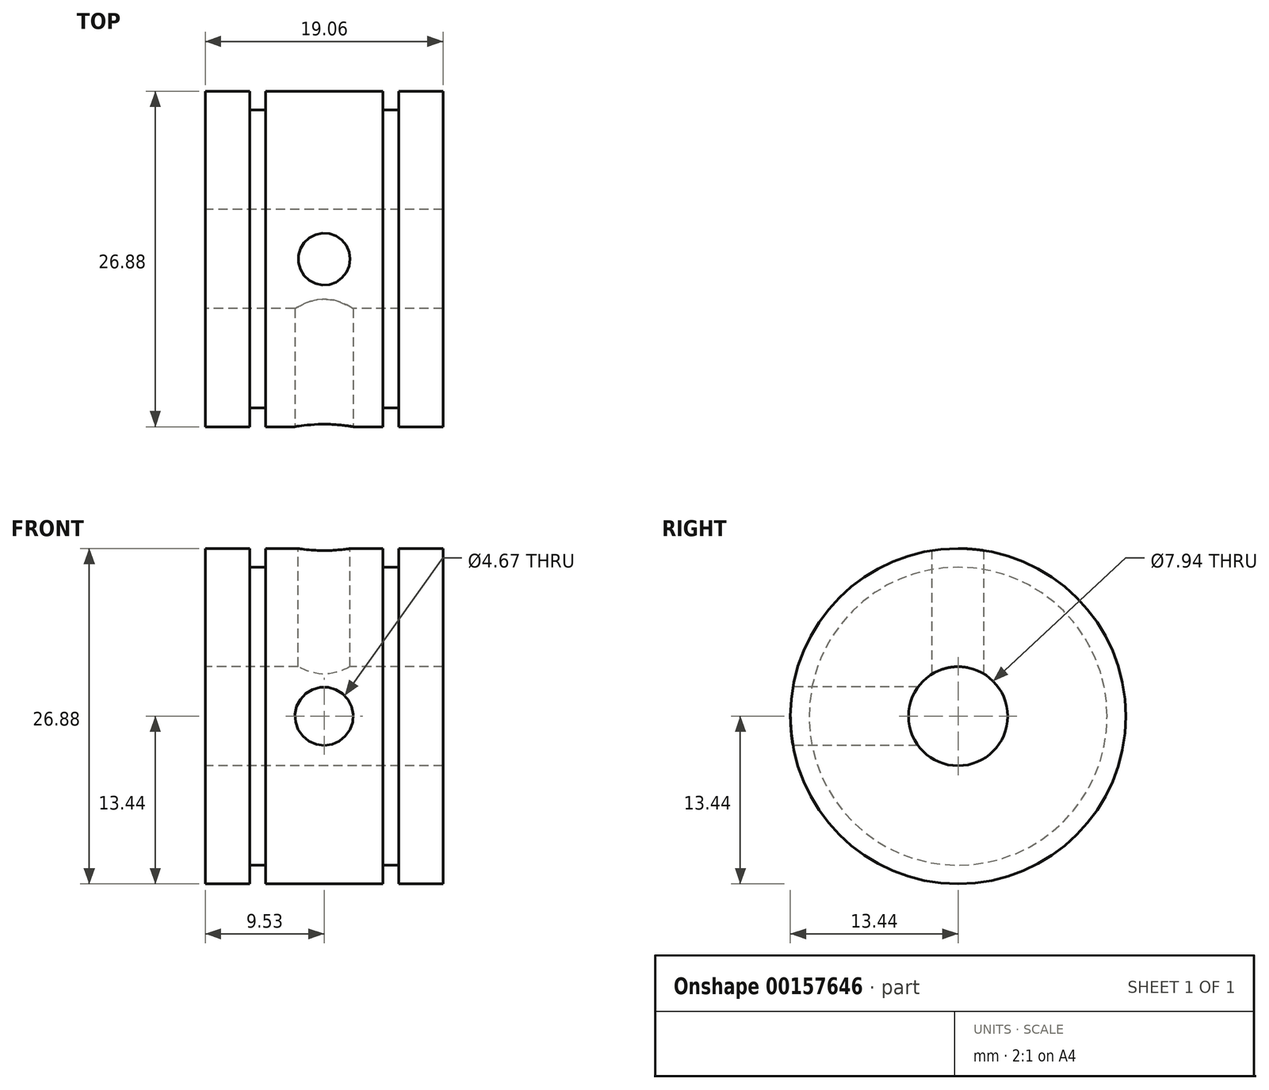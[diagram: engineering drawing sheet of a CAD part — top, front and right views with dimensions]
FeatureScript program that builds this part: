
annotation { "Feature Type Name" : "Feature", "Feature Type Description" : "" }
export const myFeature = defineFeature(function(context is Context, id is Id, definition is map)
    precondition{}
    {
        {
            var Q0;
            Q0=qCreatedBy(makeId("Right.planeOp"),FACE);
            var sketch = newSketch(context, id + "F0", { "sketchPlane" : qUnion([Q0])});
            skCircle(sketch, "E0", {"center": v(0, 0) * mm, "radius": 13.44 * mm});
            skCircle(sketch, "E1", {"center": v(0, 0) * mm, "radius": 3.97 * mm});
            skCircle(sketch, "E2", {"center": v(0, 0) * mm, "radius": 11.94 * mm});
            skSolve(sketch);
        }
        {
            var Q0;
            Q0=makeQuery(id+"F0.imprint","IMPRINT",FACE,{"disambiguationData":[TD([[makeQuery(id+"F0.imprint","IMPRINT",EDGE,{"derivedFrom":sQuery(id+"F0.wireOp",EDGE,"E0")}),1.0]])]});
            var Q1;
            Q1=makeQuery(id+"F0.imprint","IMPRINT",FACE,{"disambiguationData":[TD([[makeQuery(id+"F0.imprint","IMPRINT",EDGE,{"derivedFrom":sQuery(id+"F0.wireOp",EDGE,"E1")}),-1.0]])]});
            extrude(context, id + "F1", {"entities" : qUnion([Q0, Q1]), "depth" : 4.7 * mm});
        }
        {
            var Q0;
            Q0=makeQuery(id+"F1.opExtrude","CAP_FACE",FACE,{"disambiguationData":[OSD([sQuery(id+"F0.wireOp",EDGE,"E0"),sQuery(id+"F0.wireOp",EDGE,"E1")])],"isStart":false});
            var sketch = newSketch(context, id + "F2", { "sketchPlane" : qUnion([Q0])});
            skCircle(sketch, "E3", {"center": v(0, 0) * mm, "radius": 11.94 * mm});
            skSolve(sketch);
        }
        {
            var Q0;
            Q0=makeQuery(id+"F2.imprint","IMPRINT",FACE,{"disambiguationData":[TD([[makeQuery(id+"F2.imprint","IMPRINT",EDGE,{"derivedFrom":sQuery(id+"F2.wireOp",EDGE,"E3")}),1.0]])]});
            extrude(context, id + "F3", {"entities" : qUnion([Q0]), "operationType" : NewBodyOperationType.ADD, "depth" : 1.27 * mm});
        }
        {
            var Q0;
            Q0=makeQuery(id+"F3.opExtrude","CAP_FACE",FACE,{"disambiguationData":[OSD([sQuery(id+"F0.wireOp",EDGE,"E1"),sQuery(id+"F2.wireOp",EDGE,"E3")])],"isStart":false});
            var sketch = newSketch(context, id + "F4", { "sketchPlane" : qUnion([Q0])});
            skCircle(sketch, "E4", {"center": v(0, 0) * mm, "radius": 13.44 * mm});
            skSolve(sketch);
        }
        {
            var Q0;
            Q0=makeQuery(id+"F4.imprint","IMPRINT",FACE,{"disambiguationData":[TD([[makeQuery(id+"F4.imprint","IMPRINT",EDGE,{"derivedFrom":sQuery(id+"F4.wireOp",EDGE,"E4")}),1.0]])]});
            var Q1;
            Q1=makeQuery(id+"F4.imprint","IMPRINT",FACE,{"disambiguationData":[TD([[makeQuery(id+"F4.imprint","IMPRINT",EDGE,{"derivedFrom":makeQuery(id+"F3.opExtrude","CAP_EDGE",EDGE,{"disambiguationData":[OSD([sQuery(id+"F2.wireOp",EDGE,"E3")])],"isStart":false})}),1.0]])]});
            extrude(context, id + "F5", {"entities" : qUnion([Q0, Q1]), "operationType" : NewBodyOperationType.ADD, "depth" : 3.56 * mm});
        }
        {
            var Q0;
            Q0=makeQuery(id+"F1.opExtrude","CAP_FACE",FACE,{"disambiguationData":[OSD([sQuery(id+"F0.wireOp",EDGE,"E0"),sQuery(id+"F0.wireOp",EDGE,"E1")])],"isStart":true});
            extrude(context, id + "F6", {"entities" : qUnion([Q0]), "operationType" : NewBodyOperationType.ADD, "depth" : 4.7 * mm});
        }
        {
            var Q0;
            Q0=makeQuery(id+"F6.opExtrude","CAP_FACE",FACE,{"disambiguationData":[OSD([sQuery(id+"F0.wireOp",EDGE,"E0"),sQuery(id+"F0.wireOp",EDGE,"E1")])],"isStart":false});
            var sketch = newSketch(context, id + "F7", { "sketchPlane" : qUnion([Q0])});
            skCircle(sketch, "E5", {"center": v(0, 0) * mm, "radius": 11.94 * mm});
            skSolve(sketch);
        }
        {
            var Q0;
            Q0=makeQuery(id+"F7.imprint","IMPRINT",FACE,{"disambiguationData":[TD([[makeQuery(id+"F7.imprint","IMPRINT",EDGE,{"derivedFrom":sQuery(id+"F7.wireOp",EDGE,"E5")}),1.0]])]});
            extrude(context, id + "F8", {"entities" : qUnion([Q0]), "operationType" : NewBodyOperationType.ADD, "depth" : 1.27 * mm});
        }
        {
            var Q0;
            Q0=makeQuery(id+"F8.opExtrude","CAP_FACE",FACE,{"disambiguationData":[OSD([sQuery(id+"F0.wireOp",EDGE,"E1"),sQuery(id+"F7.wireOp",EDGE,"E5")])],"isStart":false});
            var sketch = newSketch(context, id + "F9", { "sketchPlane" : qUnion([Q0])});
            skCircle(sketch, "E6", {"center": v(0, 0) * mm, "radius": 13.44 * mm});
            skSolve(sketch);
        }
        {
            var Q0;
            Q0=makeQuery(id+"F9.imprint","IMPRINT",FACE,{"disambiguationData":[TD([[makeQuery(id+"F9.imprint","IMPRINT",EDGE,{"derivedFrom":makeQuery(id+"F8.opExtrude","CAP_EDGE",EDGE,{"disambiguationData":[OSD([sQuery(id+"F7.wireOp",EDGE,"E5")])],"isStart":false})}),1.0]])]});
            var Q1;
            Q1=makeQuery(id+"F9.imprint","IMPRINT",FACE,{"disambiguationData":[TD([[makeQuery(id+"F9.imprint","IMPRINT",EDGE,{"derivedFrom":sQuery(id+"F9.wireOp",EDGE,"E6")}),1.0]])]});
            extrude(context, id + "F10", {"entities" : qUnion([Q0, Q1]), "operationType" : NewBodyOperationType.ADD, "depth" : 3.56 * mm});
        }
        {
            var Q0;
            Q0=makeQuery(id+"F5.opExtrude","CAP_FACE",FACE,{"disambiguationData":[OSD([sQuery(id+"F0.wireOp",EDGE,"E1"),sQuery(id+"F4.wireOp",EDGE,"E4")])],"isStart":false});
            var sketch = newSketch(context, id + "F11", { "sketchPlane" : qUnion([Q0])});
            skLineSegment(sketch, "E7", {"start": v(0, 0) * mm, "end": v(0, 13.44) * mm, "construction": true});
            skLineSegment(sketch, "E8", {"start": v(0, 0) * mm, "end": v(-13.44, 0) * mm, "construction": true});
            skSolve(sketch);
        }
        {
            var Q0;
            Q0=makeQuery(id+"F10.opExtrude","CAP_FACE",FACE,{"disambiguationData":[OSD([sQuery(id+"F0.wireOp",EDGE,"E1"),sQuery(id+"F9.wireOp",EDGE,"E6")])],"isStart":false});
            var sketch = newSketch(context, id + "F12", { "sketchPlane" : qUnion([Q0])});
            skLineSegment(sketch, "E9", {"start": v(0, 0) * mm, "end": v(0, 13.44) * mm, "construction": true});
            skLineSegment(sketch, "E10", {"start": v(0, 13.44) * mm, "end": v(20.53, 13.44) * mm, "construction": true});
            skLineSegment(sketch, "E11", {"start": v(0, 0) * mm, "end": v(13.44, 0) * mm, "construction": true});
            skLineSegment(sketch, "E12", {"start": v(13.44, 0) * mm, "end": v(13.44, -13.55) * mm, "construction": true});
            skSolve(sketch);
        }
        {
            var Q0;
            Q0=sQuery(id+"F12.wireOp",VERTEX,"E10.start");
            var Q1;
            Q1=sQuery(id+"F12.wireOp",VERTEX,"E10.end");
            var Q2;
            Q2=sQuery(id+"F11.wireOp",VERTEX,"E7.end");
            cPlane(context, id + "F13", {"entities" : qUnion([Q0, Q1, Q2]), "cplaneType" : CPlaneType.THREE_POINT, "offset" : 25.4 * mm, "width" : 152.4 * mm, "height" : 152.4 * mm});
        }
        {
            var Q0;
            Q0=qCreatedBy(id+"F13.planeOp",FACE);
            var sketch = newSketch(context, id + "F14", { "sketchPlane" : qUnion([Q0])});
            skCircle(sketch, "E13", {"center": v(0, 0) * mm, "radius": 2.08 * mm});
            skSolve(sketch);
        }
        {
            var Q0;
            Q0=makeQuery(id+"F14.imprint","IMPRINT",FACE,{"disambiguationData":[TD([[makeQuery(id+"F14.imprint","IMPRINT",EDGE,{"derivedFrom":sQuery(id+"F14.wireOp",EDGE,"E13")}),1.0]])]});
            var Q1;
            Q1=sQuery(id+"F14.wireOp",EDGE,"E13");
            extrude(context, id + "F15", {"entities" : qUnion([Q0]), "operationType" : NewBodyOperationType.REMOVE, "surfaceEntities" : qUnion([Q1]), "endBound" : BoundingType.UP_TO_NEXT, "depth" : 25.4 * mm});
        }
        {
            var Q0;
            Q0=sQuery(id+"F12.wireOp",VERTEX,"E12.start");
            var Q1;
            Q1=sQuery(id+"F12.wireOp",VERTEX,"E12.end");
            var Q2;
            Q2=sQuery(id+"F11.wireOp",VERTEX,"E8.end");
            cPlane(context, id + "F16", {"entities" : qUnion([Q0, Q1, Q2]), "cplaneType" : CPlaneType.THREE_POINT, "offset" : 25.4 * mm, "width" : 152.4 * mm, "height" : 152.4 * mm});
        }
        {
            var Q0;
            Q0=qCreatedBy(id+"F16.planeOp",FACE);
            var sketch = newSketch(context, id + "F17", { "sketchPlane" : qUnion([Q0])});
            skCircle(sketch, "E14", {"center": v(0, 0) * mm, "radius": 2.34 * mm});
            skSolve(sketch);
        }
        {
            var Q0;
            Q0=makeQuery(id+"F17.imprint","IMPRINT",FACE,{"disambiguationData":[TD([[makeQuery(id+"F17.imprint","IMPRINT",EDGE,{"derivedFrom":sQuery(id+"F17.wireOp",EDGE,"E14")}),1.0]])]});
            extrude(context, id + "F18", {"entities" : qUnion([Q0]), "operationType" : NewBodyOperationType.REMOVE, "depth" : 12.7 * mm});
        }
    });
